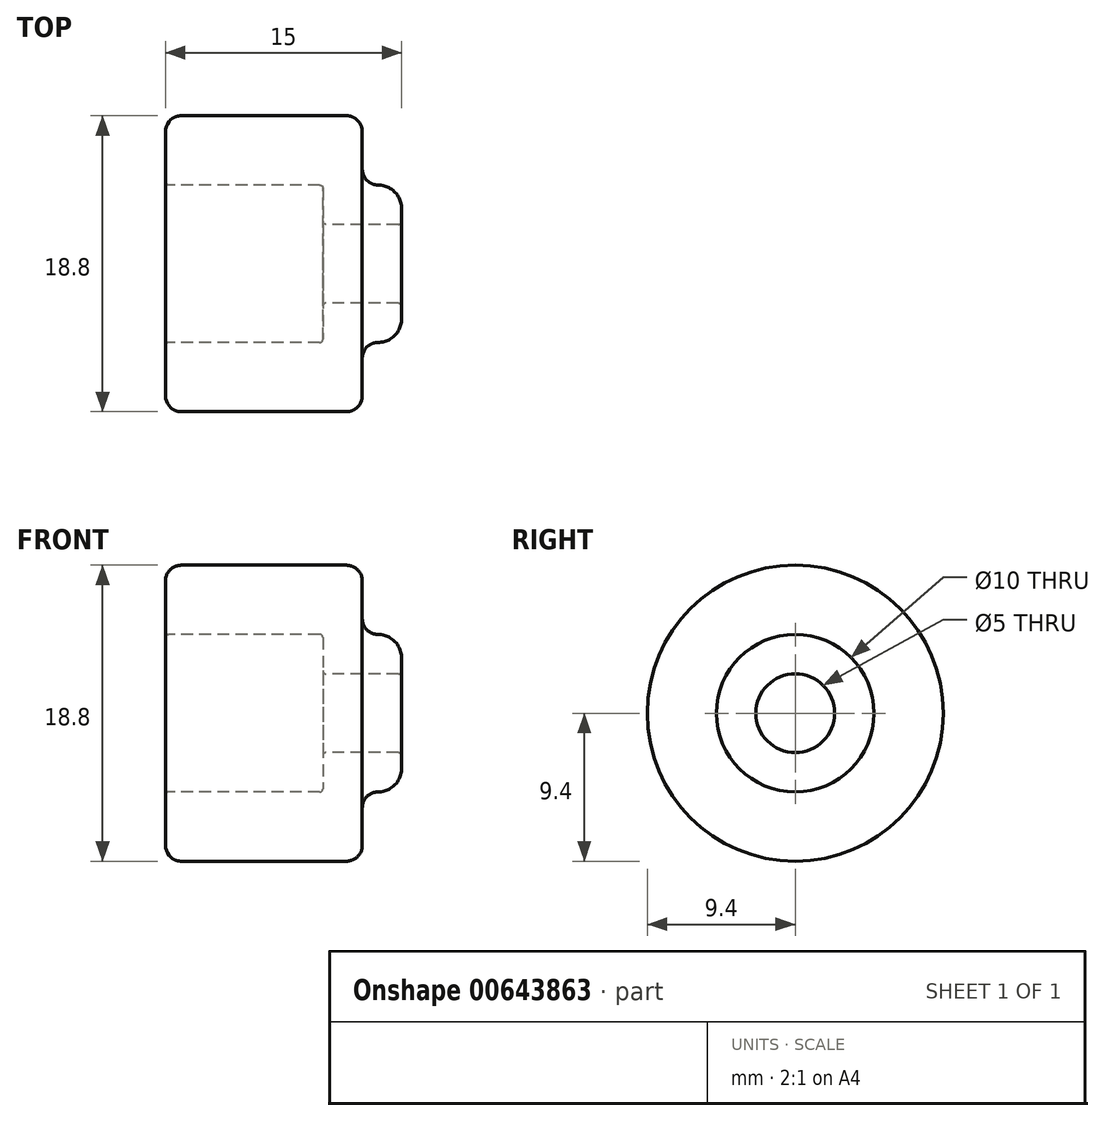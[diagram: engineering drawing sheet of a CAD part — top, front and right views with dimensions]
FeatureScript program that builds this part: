
annotation { "Feature Type Name" : "Feature", "Feature Type Description" : "" }
export const myFeature = defineFeature(function(context is Context, id is Id, definition is map)
    precondition{}
    {
        {
            var Q0;
            Q0=qCreatedBy(makeId("Front.planeOp"),FACE);
            var sketch = newSketch(context, id + "F0", { "sketchPlane" : qUnion([Q0])});
            skLineSegment(sketch, "E0", {"start": v(0, 0) * mm, "end": v(10, 0) * mm});
            skLineSegment(sketch, "E1", {"start": v(-10, 5) * mm, "end": v(-10, 0) * mm});
            skLineSegment(sketch, "E2", {"start": v(10, 0) * mm, "end": v(10, 2.5) * mm});
            skLineSegment(sketch, "E3", {"start": v(4.8, 2.5) * mm, "end": v(0.2, 2.5) * mm});
            skLineSegment(sketch, "E4", {"start": v(0, 2.7) * mm, "end": v(0, 4.8) * mm});
            skLineSegment(sketch, "E5", {"start": v(-0.2, 5) * mm, "end": v(-9.8, 5) * mm});
            skLineSegment(sketch, "E6", {"start": v(-10, 5) * mm, "end": v(-10, 5) * mm});
            skLineSegment(sketch, "E7", {"start": v(10, 2.5) * mm, "end": v(10, 2.5) * mm});
            skLineSegment(sketch, "E8", {"start": v(2.5, 6) * mm, "end": v(2.5, 8.4) * mm});
            skLineSegment(sketch, "E9", {"start": v(-10, 5.2) * mm, "end": v(-10, 8.4) * mm});
            skArc(sketch, "E10.filletArc", {"start": v(-9, 9.4) * mm, "mid": v(-9.7, 9.1) * mm, "end": v(-10, 8.4) * mm});
            skPoint(sketch, "E11.visualSharp", {"position": v(-10, 5) * mm});
            skArc(sketch, "E11.filletArc", {"start": v(-10, 5.2) * mm, "mid": v(-9.94, 5.06) * mm, "end": v(-9.8, 5) * mm});
            skArc(sketch, "E12.filletArc", {"start": v(2.5, 8.4) * mm, "mid": v(2.2, 9.1) * mm, "end": v(1.5, 9.4) * mm});
            skArc(sketch, "E13.filletArc", {"start": v(2.5, 6) * mm, "mid": v(2.8, 5.3) * mm, "end": v(3.5, 5) * mm});
            skPoint(sketch, "E14.visualSharp", {"position": v(10, 2.5) * mm});
            skArc(sketch, "E14.filletArc", {"start": v(4.8, 2.5) * mm, "mid": v(4.94, 2.56) * mm, "end": v(5, 2.7) * mm});
            skLineSegment(sketch, "E15", {"start": v(-9, 9.4) * mm, "end": v(1.5, 9.4) * mm});
            skPoint(sketch, "E16.visualSharp", {"position": v(0, 5) * mm});
            skArc(sketch, "E16.filletArc", {"start": v(0, 4.8) * mm, "mid": v(-0.06, 4.94) * mm, "end": v(-0.2, 5) * mm});
            skPoint(sketch, "E17.visualSharp", {"position": v(0, 2.5) * mm});
            skArc(sketch, "E17.filletArc", {"start": v(0, 2.7) * mm, "mid": v(0.06, 2.56) * mm, "end": v(0.2, 2.5) * mm});
            skLineSegment(sketch, "E18", {"start": v(3.5, 5) * mm, "end": v(3.5, 5) * mm});
            skLineSegment(sketch, "E19", {"start": v(5, 3.5) * mm, "end": v(5, 2.7) * mm});
            skPoint(sketch, "E20.visualSharp", {"position": v(5, 5) * mm});
            skArc(sketch, "E20.filletArc", {"start": v(5, 3.5) * mm, "mid": v(4.56, 4.56) * mm, "end": v(3.5, 5) * mm});
            skSolve(sketch);
        }
        {
            var Q0;
            Q0 = qSketchRegion(id + "F0", true);
            var Q1;
            Q1=sQuery(id+"F0.wireOp",EDGE,"E0");
            revolve(context, id + "F1", {"entities" : qUnion([Q0]), "axis" : qUnion([Q1]), "revolveType" : RevolveType.FULL});
        }
    });
